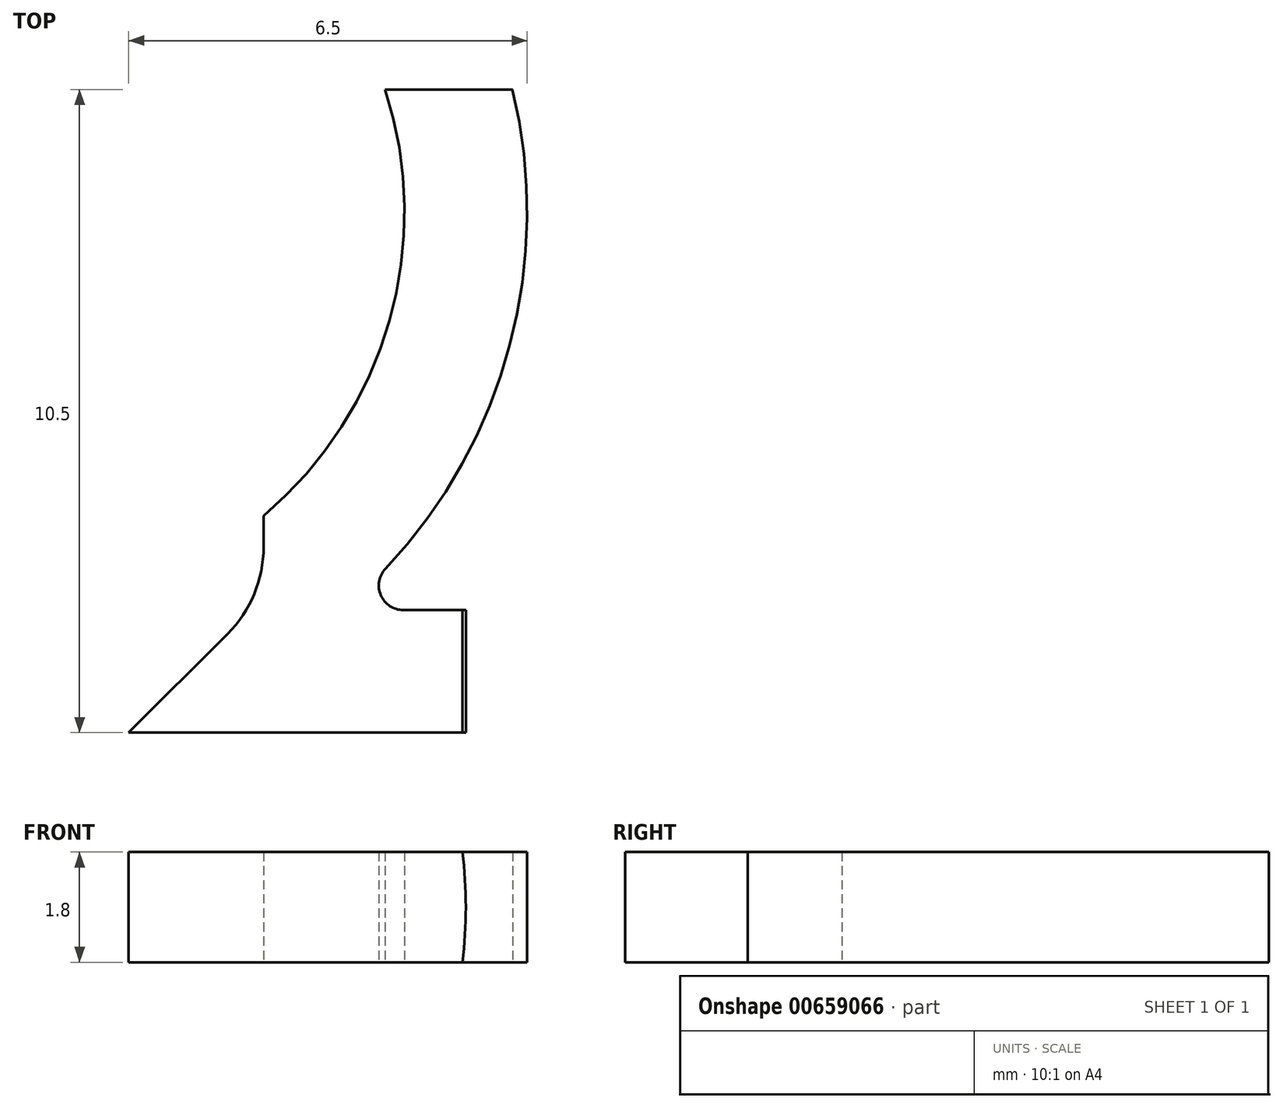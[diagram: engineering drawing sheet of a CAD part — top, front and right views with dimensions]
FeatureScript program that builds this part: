
annotation { "Feature Type Name" : "Feature", "Feature Type Description" : "" }
export const myFeature = defineFeature(function(context is Context, id is Id, definition is map)
    precondition{}
    {
        {
            var Q0;
            Q0=qCreatedBy(makeId("Top.planeOp"),FACE);
            var sketch = newSketch(context, id + "F0", { "sketchPlane" : qUnion([Q0])});
            skLineSegment(sketch, "E0", {"start": v(0, 0) * mm, "end": v(2, 0) * mm, "construction": true});
            skLineSegment(sketch, "E1", {"start": v(7.5, 0) * mm, "end": v(7.5, 2) * mm});
            skLineSegment(sketch, "E2", {"start": v(8.5, 8.5) * mm, "end": v(6.5, 8.5) * mm});
            skLineSegment(sketch, "E3", {"start": v(6.5, 8.5) * mm, "end": v(6.5, 8.5) * mm});
            skLineSegment(sketch, "E4", {"start": v(0, 2) * mm, "end": v(0, 2) * mm});
            skLineSegment(sketch, "E5", {"start": v(0, 2) * mm, "end": v(0, 0) * mm, "construction": true});
            skPoint(sketch, "E6.visualSharp", {"position": v(6.5, 2) * mm});
            skArc(sketch, "E6.filletArc", {"start": v(0, 2) * mm, "mid": v(1.01, 2.08) * mm, "end": v(2, 2.32) * mm, "construction": true});
            skArc(sketch, "E7.0", {"start": v(0, 0) * mm, "mid": v(2.92, 0.52) * mm, "end": v(5.48, 2) * mm, "construction": true});
            skLineSegment(sketch, "E8", {"start": v(0, 2) * mm, "end": v(5.48, 2) * mm, "construction": true});
            skLineSegment(sketch, "E9", {"start": v(6.48, 2) * mm, "end": v(7.5, 2) * mm});
            skArc(sketch, "E10", {"start": v(6.19, 2.67) * mm, "mid": v(8.22, 6.32) * mm, "end": v(8.26, 10.5) * mm});
            skLineSegment(sketch, "E11", {"start": v(2, 0) * mm, "end": v(2, 2.32) * mm, "construction": true});
            skArc(sketch, "E12", {"start": v(2, 2.32) * mm, "mid": v(3.16, 2.82) * mm, "end": v(4.2, 3.54) * mm, "construction": true});
            skLineSegment(sketch, "E13", {"start": v(2, 0) * mm, "end": v(7.5, 0) * mm});
            skLineSegment(sketch, "E14", {"start": v(6.18, 10.5) * mm, "end": v(8.26, 10.5) * mm});
            skLineSegment(sketch, "E15", {"start": v(2, 0) * mm, "end": v(3.61, 1.61) * mm});
            skLineSegment(sketch, "E16", {"start": v(4.2, 3.03) * mm, "end": v(4.2, 3.54) * mm});
            skPoint(sketch, "E17.visualSharp", {"position": v(4.2, 2.2) * mm});
            skArc(sketch, "E17.filletArc", {"start": v(3.61, 1.61) * mm, "mid": v(4.05, 2.26) * mm, "end": v(4.2, 3.03) * mm});
            skLineSegment(sketch, "E18", {"start": v(4.2, 3.54) * mm, "end": v(4.2, 3.54) * mm});
            skArc(sketch, "E19", {"start": v(4.2, 3.54) * mm, "mid": v(6.25, 6.72) * mm, "end": v(6.18, 10.5) * mm});
            skPoint(sketch, "E20.visualSharp", {"position": v(5.48, 2) * mm});
            skArc(sketch, "E20.filletArc", {"start": v(6.19, 2.67) * mm, "mid": v(6.11, 2.24) * mm, "end": v(6.48, 2) * mm});
            skSolve(sketch);
        }
        {
            var Q0;
            Q0=qSketchRegion(id+"F0",true);
            extrude(context, id + "F1", {"entities" : qUnion([Q0]), "endBound" : BoundingType.SYMMETRIC, "depth" : 1.8 * mm, "offsetDistance" : 25 * mm});
        }
        {
            var Q0;
            Q0=makeQuery(id+"F1.opExtrude","SWEPT_FACE",FACE,{"disambiguationData":[OSD([sQuery(id+"F0.wireOp",EDGE,"E13")])]});
            var sketch = newSketch(context, id + "F2", { "sketchPlane" : qUnion([Q0])});
            skCircle(sketch, "E21", {"center": v(0, 0) * mm, "radius": 7.5 * mm});
            skCircle(sketch, "E22", {"center": v(0, 0) * mm, "radius": 8 * mm});
            skSolve(sketch);
        }
        {
            var Q0;
            Q0=qSketchRegion(id+"F2",true);
            var Q1;
            Q1=makeQuery(id+"F1.opExtrude","SWEPT_FACE",FACE,{"disambiguationData":[OSD([sQuery(id+"F0.wireOp",EDGE,"E9")])]});
            extrude(context, id + "F3", {"entities" : qUnion([Q0]), "operationType" : NewBodyOperationType.REMOVE, "endBound" : BoundingType.UP_TO_SURFACE, "oppositeDirection" : true, "depth" : 25 * mm, "endBoundEntityFace" : qUnion([Q1]), "offsetDistance" : 25 * mm});
        }
    });
